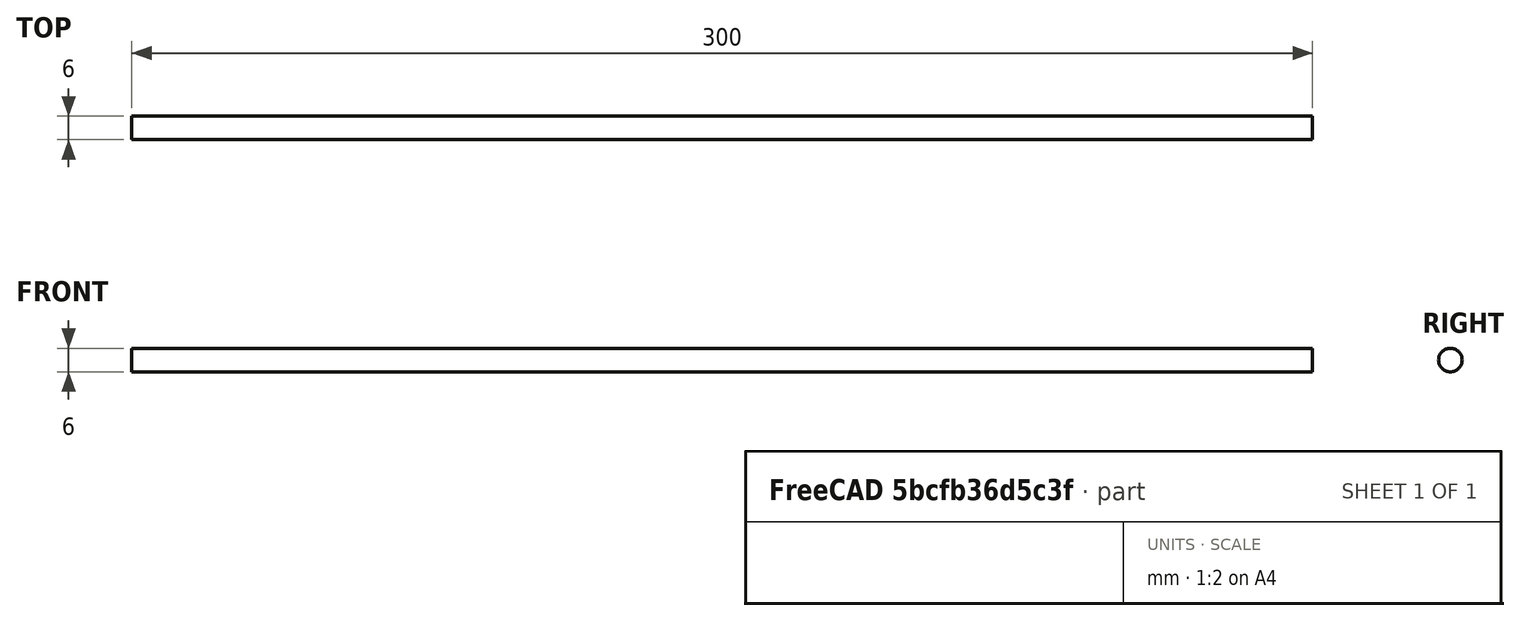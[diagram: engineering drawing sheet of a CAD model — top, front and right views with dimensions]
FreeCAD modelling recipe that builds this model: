
FCSTD DOCUMENT  (FreeCAD 0.19R18028 (Git))
Label: upper-stage-actuator-rod
License: Public Domain
LicenseURL: http://en.wikipedia.org/wiki/Public_domain
objects: Part::FeaturePython×6, App::FeaturePython×2, Sketcher::SketchObject×1, PartDesign::Pad×1, PartDesign::Body×1
note: 9 computed .brp shape members not serialized (recipe doc carries the construction recipe); baked Part::Feature solids carry a one-line shape summary decoded from their .brp

FEATURE [Sketcher::SketchObject] Sketch
  MapMode = 5
  Placement = pos=(0,0,0) rot=(0.57735,0.57735,0.57735;2.0944rad)
  Support = -> [YZ_Plane]
  sketch-geometry (1):
    g0: Circle CenterX=0 CenterY=0 CenterZ=0 NormalX=0 NormalY=0 NormalZ=1 AngleXU=0 Radius=3
  constraints (2):
    c: Coincident(g0,g-1)
    c: Radius(g0) = 3
FEATURE [PartDesign::Pad] Pad
  ClaimChildren = false
  Length = 300
  Length2 = 100
  Midplane = true
  Placement = pos=(0,0,0) rot=(0.57735,0.57735,0.57735;2.0944rad)
  Profile = -> Sketch
  Type = 0
FEATURE [PartDesign::Body] Body
  Group = -> [Sketch,Pad]
  Origin = -> Origin
  Tip = -> Pad
FEATURE [App::FeaturePython] Constraints  # WARN: FeaturePython — macro-defined, semantics opaque (R4)
  GroupMode = 1
  _Version = 1
FEATURE [Part::FeaturePython] Parts  # WARN: FeaturePython — macro-defined, semantics opaque (R4)
  Group = -> [Body]
  GroupMode = 0
FEATURE [Part::FeaturePython] Assembly  label="upper-stage-actuator-rod"  # WARN: FeaturePython — macro-defined, semantics opaque (R4)
  AutoRelax = true
  BuildShape = 0
  Freeze = false
  Group = -> [Constraints,Elements,Parts]
  GroupMode = 1
  SolverType = 1
  Verbose = false
  _SolverType = 1
  _Version = 1
FEATURE [App::FeaturePython] Elements  # WARN: FeaturePython — macro-defined, semantics opaque (R4)
  Group = -> [Element,Element001,Element002,Element003]
  GroupMode = 1
FEATURE [Part::FeaturePython] Element  label="middle"  # link proxy (typed FeaturePython)
  Detach = false
  LinkTransform = true
  LinkedObject = -> Body [Pad.Sketch.Edge1]
  _Parent = -> Elements
FEATURE [Part::FeaturePython] Element001  label="left"  # link proxy (typed FeaturePython)
  Detach = false
  LinkTransform = true
  LinkedObject = -> Body [Pad.Edge2]
  _Parent = -> Elements
FEATURE [Part::FeaturePython] Element002  label="right"  # link proxy (typed FeaturePython)
  Detach = false
  LinkTransform = true
  LinkedObject = -> Body [Pad.Edge3]
  _Parent = -> Elements
FEATURE [Part::FeaturePython] Element003  # link proxy (typed FeaturePython)
  Detach = false
  LinkTransform = true
  LinkedObject = -> Body [Pad.Edge1]
  _Parent = -> Elements
